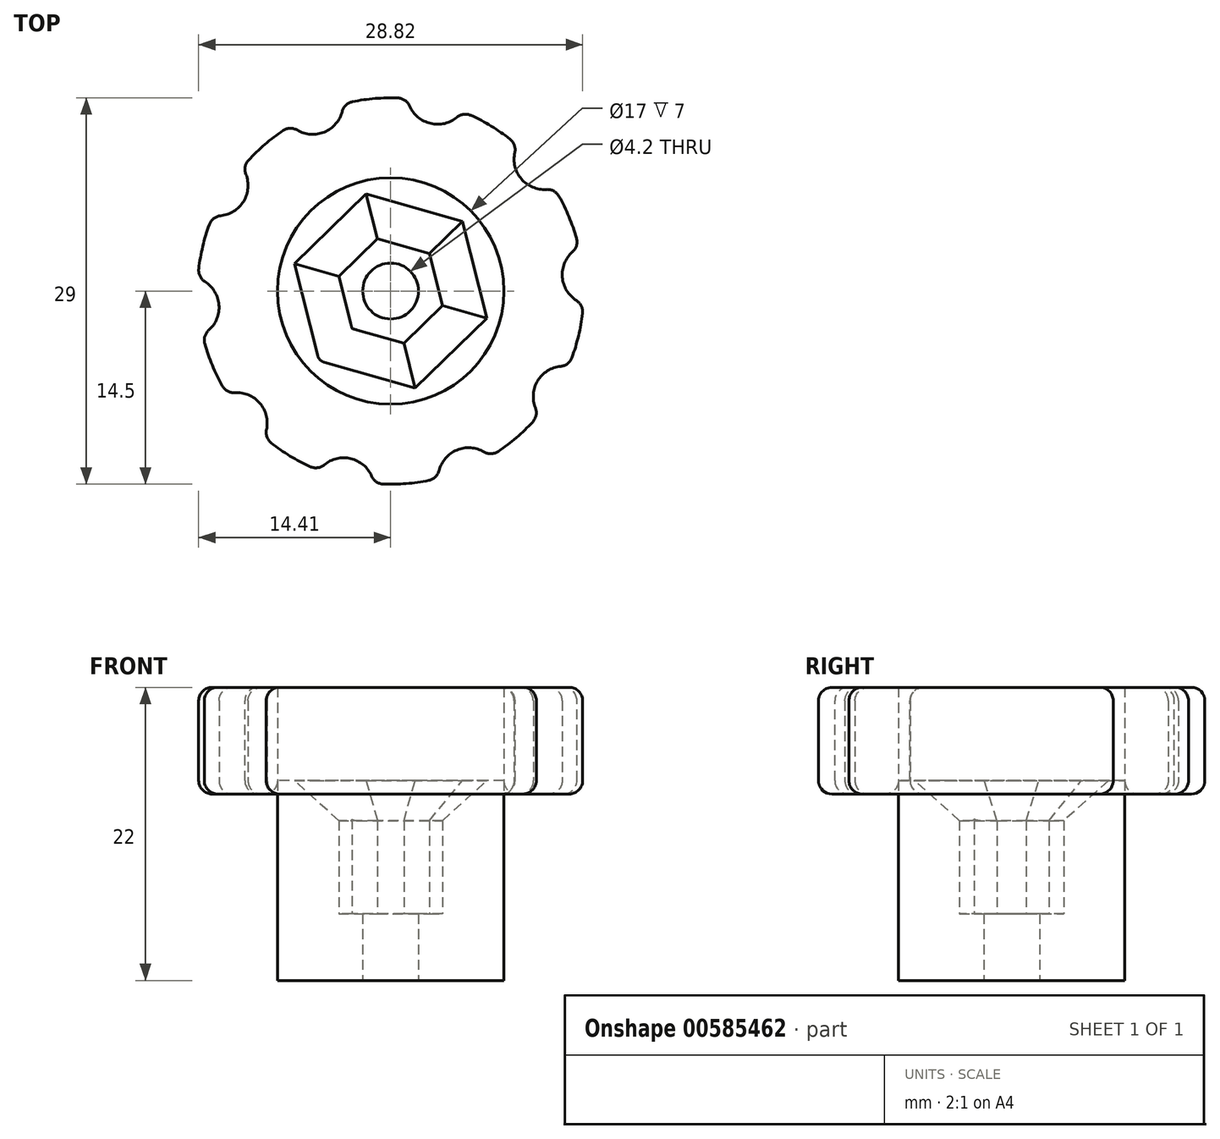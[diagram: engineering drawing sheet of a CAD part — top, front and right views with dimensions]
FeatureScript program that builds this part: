
annotation { "Feature Type Name" : "Feature", "Feature Type Description" : "" }
export const myFeature = defineFeature(function(context is Context, id is Id, definition is map)
    precondition{}
    {
        {
            var Q0;
            Q0=qCreatedBy(makeId("Top.planeOp"),FACE);
            var sketch = newSketch(context, id + "F0", { "sketchPlane" : qUnion([Q0])});
            skCircle(sketch, "E0", {"center": v(0, 0) * mm, "radius": 8.5 * mm});
            skCircle(sketch, "E1", {"center": v(0, 0) * mm, "radius": 2.1 * mm});
            skSolve(sketch);
        }
        {
            var Q0;
            Q0=makeQuery(id+"F0.imprint","IMPRINT",FACE,{"disambiguationData":[TD([[makeQuery(id+"F0.imprint","IMPRINT",EDGE,{"derivedFrom":sQuery(id+"F0.wireOp",EDGE,"E0")}),1.0]])]});
            extrude(context, id + "F1", {"entities" : qUnion([Q0]), "depth" : 5 * mm, "offsetDistance" : 25 * mm});
        }
        {
            var Q0;
            Q0=makeQuery(id+"F1.opExtrude","CAP_FACE",FACE,{"disambiguationData":[OSD([sQuery(id+"F0.wireOp",EDGE,"E0"),sQuery(id+"F0.wireOp",EDGE,"E1")])],"isStart":false});
            var sketch = newSketch(context, id + "F2", { "sketchPlane" : qUnion([Q0])});
            skCircle(sketch, "E2.cCircle", {"center": v(0, 0) * mm, "radius": 3.5 * mm, "construction": true});
            skLineSegment(sketch, "E2.0", {"start": v(3.89, -1.1) * mm, "end": v(0.99, -3.92) * mm});
            skLineSegment(sketch, "E2.1", {"start": v(0.99, -3.92) * mm, "end": v(-2.9, -2.82) * mm});
            skLineSegment(sketch, "E2.2", {"start": v(-2.9, -2.82) * mm, "end": v(-3.89, 1.1) * mm});
            skLineSegment(sketch, "E2.3", {"start": v(-3.89, 1.1) * mm, "end": v(-0.99, 3.92) * mm});
            skLineSegment(sketch, "E2.4", {"start": v(-0.99, 3.92) * mm, "end": v(2.9, 2.82) * mm});
            skLineSegment(sketch, "E2.5", {"start": v(2.9, 2.82) * mm, "end": v(3.89, -1.1) * mm});
            skPoint(sketch, "E2.0.midPoint", {"position": v(2.44, -2.51) * mm});
            skCircle(sketch, "E3", {"center": v(0, 0) * mm, "radius": 8.5 * mm});
            skSolve(sketch);
        }
        {
            var Q0;
            Q0=makeQuery(id+"F2.imprint","IMPRINT",FACE,{"disambiguationData":[TD([[makeQuery(id+"F2.imprint","IMPRINT",EDGE,{"derivedFrom":sQuery(id+"F2.wireOp",EDGE,"E2.0")}),1.0]])]});
            extrude(context, id + "F3", {"entities" : qUnion([Q0]), "operationType" : NewBodyOperationType.ADD, "depth" : 10 * mm, "offsetDistance" : 25 * mm});
        }
        {
            var Q0;
            Q0=makeQuery(id+"F3.opExtrude","CAP_FACE",FACE,{"disambiguationData":[OSD([sQuery(id+"F2.wireOp",EDGE,"E2.0"),sQuery(id+"F2.wireOp",EDGE,"E2.1"),sQuery(id+"F2.wireOp",EDGE,"E2.2"),sQuery(id+"F2.wireOp",EDGE,"E2.3"),sQuery(id+"F2.wireOp",EDGE,"E2.4"),sQuery(id+"F2.wireOp",EDGE,"E2.5"),sQuery(id+"F2.wireOp",EDGE,"E3")])],"isStart":false});
            var sketch = newSketch(context, id + "F4", { "sketchPlane" : qUnion([Q0])});
            skArc(sketch, "E4", {"start": v(-7.47, 12.43) * mm, "mid": v(-9.44, 11) * mm, "end": v(-11.15, 9.27) * mm});
            skCircle(sketch, "E5", {"center": v(0, 0) * mm, "radius": 5 * mm});
            skArc(sketch, "E6", {"start": v(-7.47, 12.43) * mm, "mid": v(-4.97, 11.94) * mm, "end": v(-3.57, 14.05) * mm});
            skArc(sketch, "E7.1.0", {"start": v(-13.35, 5.67) * mm, "mid": v(-11.04, 6.73) * mm, "end": v(-11.15, 9.27) * mm});
            skArc(sketch, "E7.2.0", {"start": v(-14.13, -3.26) * mm, "mid": v(-12.89, -1.04) * mm, "end": v(-14.47, 0.95) * mm});
            skArc(sketch, "E7.3.0", {"start": v(-9.52, -10.94) * mm, "mid": v(-9.82, -8.42) * mm, "end": v(-12.26, -7.73) * mm});
            skArc(sketch, "E7.4.0", {"start": v(-1.27, -14.44) * mm, "mid": v(-3, -12.58) * mm, "end": v(-5.38, -13.47) * mm});
            skArc(sketch, "E7.5.0", {"start": v(7.47, -12.43) * mm, "mid": v(4.97, -11.94) * mm, "end": v(3.57, -14.05) * mm});
            skArc(sketch, "E7.6.0", {"start": v(13.35, -5.67) * mm, "mid": v(11.04, -6.73) * mm, "end": v(11.15, -9.27) * mm});
            skArc(sketch, "E7.7.0", {"start": v(14.13, 3.26) * mm, "mid": v(12.89, 1.04) * mm, "end": v(14.47, -0.95) * mm});
            skArc(sketch, "E7.8.0", {"start": v(9.52, 10.94) * mm, "mid": v(9.82, 8.42) * mm, "end": v(12.26, 7.73) * mm});
            skArc(sketch, "E7.9.0", {"start": v(1.27, 14.44) * mm, "mid": v(3, 12.58) * mm, "end": v(5.38, 13.47) * mm});
            skArc(sketch, "E8.trimOffspring", {"start": v(1.27, 14.44) * mm, "mid": v(-1.17, 14.45) * mm, "end": v(-3.57, 14.05) * mm});
            skArc(sketch, "E9.trimOffspring", {"start": v(9.52, 10.94) * mm, "mid": v(7.55, 12.38) * mm, "end": v(5.38, 13.47) * mm});
            skArc(sketch, "E10.trimOffspring", {"start": v(14.13, 3.26) * mm, "mid": v(13.39, 5.58) * mm, "end": v(12.26, 7.73) * mm});
            skArc(sketch, "E11.trimOffspring", {"start": v(13.35, -5.67) * mm, "mid": v(14.1, -3.36) * mm, "end": v(14.47, -0.95) * mm});
            skArc(sketch, "E12.trimOffspring", {"start": v(7.47, -12.43) * mm, "mid": v(9.44, -11) * mm, "end": v(11.15, -9.27) * mm});
            skArc(sketch, "E13.trimOffspring", {"start": v(-1.27, -14.44) * mm, "mid": v(1.17, -14.45) * mm, "end": v(3.57, -14.05) * mm});
            skArc(sketch, "E14.trimOffspring", {"start": v(-9.52, -10.94) * mm, "mid": v(-7.55, -12.38) * mm, "end": v(-5.38, -13.47) * mm});
            skArc(sketch, "E15.trimOffspring", {"start": v(-14.13, -3.26) * mm, "mid": v(-13.39, -5.58) * mm, "end": v(-12.26, -7.73) * mm});
            skArc(sketch, "E16.trimOffspring", {"start": v(-13.35, 5.67) * mm, "mid": v(-14.1, 3.36) * mm, "end": v(-14.47, 0.95) * mm});
            skSolve(sketch);
        }
        {
            var Q0;
            Q0=makeQuery(id+"F4.imprint","IMPRINT",FACE,{"disambiguationData":[TD([[makeQuery(id+"F4.imprint","IMPRINT",EDGE,{"derivedFrom":sQuery(id+"F4.wireOp",EDGE,"E4")}),1.0]])]});
            extrude(context, id + "F5", {"entities" : qUnion([Q0]), "depth" : 7 * mm, "offsetDistance" : 25 * mm, "hasSecondDirection" : true, "secondDirectionOppositeDirection" : true, "secondDirectionDepth" : 1 * mm});
        }
        {
            var Q0;
            Q0=makeQuery(id+"F3.opExtrude","CAP_EDGE",EDGE,{"disambiguationData":[OSD([sQuery(id+"F2.wireOp",EDGE,"E2.2")])],"isStart":false});
            var Q1;
            Q1=makeQuery(id+"F3.opExtrude","CAP_EDGE",EDGE,{"disambiguationData":[OSD([sQuery(id+"F2.wireOp",EDGE,"E2.3")])],"isStart":false});
            var Q2;
            Q2=makeQuery(id+"F3.opExtrude","CAP_EDGE",EDGE,{"disambiguationData":[OSD([sQuery(id+"F2.wireOp",EDGE,"E2.4")])],"isStart":false});
            var Q3;
            Q3=makeQuery(id+"F3.opExtrude","CAP_EDGE",EDGE,{"disambiguationData":[OSD([sQuery(id+"F2.wireOp",EDGE,"E2.1")])],"isStart":false});
            var Q4;
            Q4=makeQuery(id+"F3.opExtrude","CAP_EDGE",EDGE,{"disambiguationData":[OSD([sQuery(id+"F2.wireOp",EDGE,"E2.0")])],"isStart":false});
            var Q5;
            Q5=makeQuery(id+"F3.opExtrude","CAP_EDGE",EDGE,{"disambiguationData":[OSD([sQuery(id+"F2.wireOp",EDGE,"E2.5")])],"isStart":false});
            chamfer(context, id + "F6", {"entities" : qUnion([Q0, Q1, Q2, Q3, Q4, Q5]), "width" : 3 * mm, "tangentPropagation" : true});
        }
        {
            var Q0;
            Q0=makeQuery(id+"F5.opExtrude","SWEPT_FACE",FACE,{"disambiguationData":[OSD([sQuery(id+"F4.wireOp",EDGE,"E6")])]});
            var Q1;
            Q1=makeQuery(id+"F5.opExtrude","SWEPT_FACE",FACE,{"disambiguationData":[OSD([sQuery(id+"F4.wireOp",EDGE,"E7.9.0")])]});
            var Q2;
            Q2=makeQuery(id+"F5.opExtrude","SWEPT_FACE",FACE,{"disambiguationData":[OSD([sQuery(id+"F4.wireOp",EDGE,"E7.8.0")])]});
            var Q3;
            Q3=makeQuery(id+"F5.opExtrude","SWEPT_FACE",FACE,{"disambiguationData":[OSD([sQuery(id+"F4.wireOp",EDGE,"E7.7.0")])]});
            var Q4;
            Q4=makeQuery(id+"F5.opExtrude","SWEPT_EDGE",EDGE,{"disambiguationData":[OSD([sQuery(id+"F4.wireOp",EDGE,"E7.6.0"),sQuery(id+"F4.wireOp",EDGE,"E12.trimOffspring")])]});
            var Q5;
            Q5=makeQuery(id+"F5.opExtrude","SWEPT_FACE",FACE,{"disambiguationData":[OSD([sQuery(id+"F4.wireOp",EDGE,"E7.1.0")])]});
            var Q6;
            Q6=makeQuery(id+"F6.opChamfer","BLEND_EDGE",EDGE,{"blendedFrom":[makeQuery(id+"F3.opExtrude","CAP_EDGE",EDGE,{"disambiguationData":[OSD([sQuery(id+"F2.wireOp",EDGE,"E2.1")])],"isStart":false}),makeQuery(id+"F3.opExtrude","CAP_EDGE",EDGE,{"disambiguationData":[OSD([sQuery(id+"F2.wireOp",EDGE,"E2.2")])],"isStart":false})],"blendedInto":[]});
            var Q7;
            Q7=makeQuery(id+"F5.opExtrude","SWEPT_FACE",FACE,{"disambiguationData":[OSD([sQuery(id+"F4.wireOp",EDGE,"E7.2.0")])]});
            var Q8;
            Q8=makeQuery(id+"F5.opExtrude","SWEPT_FACE",FACE,{"disambiguationData":[OSD([sQuery(id+"F4.wireOp",EDGE,"E7.4.0")])]});
            var Q9;
            Q9=makeQuery(id+"F5.opExtrude","SWEPT_FACE",FACE,{"disambiguationData":[OSD([sQuery(id+"F4.wireOp",EDGE,"E7.5.0")])]});
            var Q10;
            Q10=makeQuery(id+"F5.opExtrude","SWEPT_FACE",FACE,{"disambiguationData":[OSD([sQuery(id+"F4.wireOp",EDGE,"E7.3.0")])]});
            var Q11;
            Q11=makeQuery(id+"F5.opExtrude","SWEPT_FACE",FACE,{"disambiguationData":[OSD([sQuery(id+"F4.wireOp",EDGE,"E7.6.0")])]});
            var Q12;
            Q12=makeQuery(id+"F5.opExtrude","CAP_EDGE",EDGE,{"disambiguationData":[OSD([sQuery(id+"F4.wireOp",EDGE,"E10.trimOffspring")])],"isStart":false});
            var Q13;
            Q13=makeQuery(id+"F5.opExtrude","CAP_EDGE",EDGE,{"disambiguationData":[OSD([sQuery(id+"F4.wireOp",EDGE,"E9.trimOffspring")])],"isStart":false});
            var Q14;
            Q14=makeQuery(id+"F5.opExtrude","CAP_EDGE",EDGE,{"disambiguationData":[OSD([sQuery(id+"F4.wireOp",EDGE,"E8.trimOffspring")])],"isStart":false});
            var Q15;
            Q15=makeQuery(id+"F5.opExtrude","CAP_EDGE",EDGE,{"disambiguationData":[OSD([sQuery(id+"F4.wireOp",EDGE,"E4")])],"isStart":false});
            var Q16;
            Q16=makeQuery(id+"F5.opExtrude","CAP_EDGE",EDGE,{"disambiguationData":[OSD([sQuery(id+"F4.wireOp",EDGE,"E16.trimOffspring")])],"isStart":false});
            var Q17;
            Q17=makeQuery(id+"F5.opExtrude","CAP_EDGE",EDGE,{"disambiguationData":[OSD([sQuery(id+"F4.wireOp",EDGE,"E15.trimOffspring")])],"isStart":false});
            var Q18;
            Q18=makeQuery(id+"F5.opExtrude","CAP_EDGE",EDGE,{"disambiguationData":[OSD([sQuery(id+"F4.wireOp",EDGE,"E14.trimOffspring")])],"isStart":false});
            var Q19;
            Q19=makeQuery(id+"F5.opExtrude","CAP_EDGE",EDGE,{"disambiguationData":[OSD([sQuery(id+"F4.wireOp",EDGE,"E13.trimOffspring")])],"isStart":false});
            var Q20;
            Q20=makeQuery(id+"F5.opExtrude","CAP_EDGE",EDGE,{"disambiguationData":[OSD([sQuery(id+"F4.wireOp",EDGE,"E12.trimOffspring")])],"isStart":false});
            var Q21;
            Q21=makeQuery(id+"F5.opExtrude","CAP_EDGE",EDGE,{"disambiguationData":[OSD([sQuery(id+"F4.wireOp",EDGE,"E11.trimOffspring")])],"isStart":false});
            var Q22;
            Q22=makeQuery(id+"F5.opExtrude","CAP_FACE",FACE,{"disambiguationData":[OSD([sQuery(id+"F2.wireOp",EDGE,"E3"),sQuery(id+"F4.wireOp",EDGE,"E4"),sQuery(id+"F4.wireOp",EDGE,"E6"),sQuery(id+"F4.wireOp",EDGE,"E7.1.0"),sQuery(id+"F4.wireOp",EDGE,"E7.2.0"),sQuery(id+"F4.wireOp",EDGE,"E7.3.0"),sQuery(id+"F4.wireOp",EDGE,"E7.4.0"),sQuery(id+"F4.wireOp",EDGE,"E7.5.0"),sQuery(id+"F4.wireOp",EDGE,"E7.6.0"),sQuery(id+"F4.wireOp",EDGE,"E7.7.0"),sQuery(id+"F4.wireOp",EDGE,"E7.8.0"),sQuery(id+"F4.wireOp",EDGE,"E7.9.0"),sQuery(id+"F4.wireOp",EDGE,"E8.trimOffspring"),sQuery(id+"F4.wireOp",EDGE,"E9.trimOffspring"),sQuery(id+"F4.wireOp",EDGE,"E10.trimOffspring"),sQuery(id+"F4.wireOp",EDGE,"E11.trimOffspring"),sQuery(id+"F4.wireOp",EDGE,"E12.trimOffspring"),sQuery(id+"F4.wireOp",EDGE,"E13.trimOffspring"),sQuery(id+"F4.wireOp",EDGE,"E14.trimOffspring"),sQuery(id+"F4.wireOp",EDGE,"E15.trimOffspring"),sQuery(id+"F4.wireOp",EDGE,"E16.trimOffspring")])],"isStart":true});
            fillet(context, id + "F7", {"entities" : qUnion([Q0, Q1, Q2, Q3, Q4, Q5, Q6, Q7, Q8, Q9, Q10, Q11, Q12, Q13, Q14, Q15, Q16, Q17, Q18, Q19, Q20, Q21, Q22]), "radius" : 1 * mm, "tangentPropagation" : true, "allowEdgeOverflow" : false});
        }
    });
